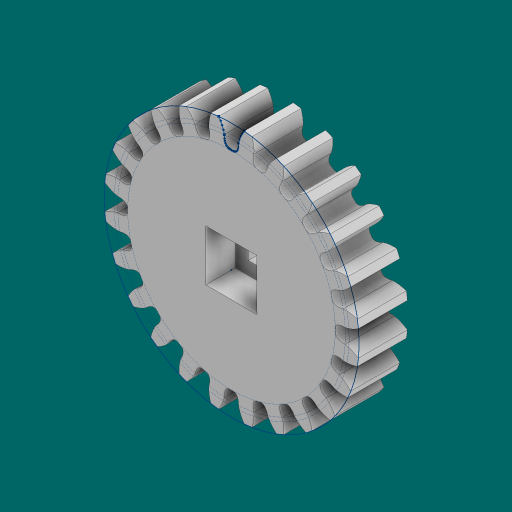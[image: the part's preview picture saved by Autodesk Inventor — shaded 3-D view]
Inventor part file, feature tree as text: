
AUTODESK INVENTOR PART (.ipt)
format: ipt  version: 2023.1 (Build 271208000, 208)  size: 313,856 bytes
history: native  units: in
note: dims shown in document units (in); Inventor stores cm internally (conversion verified against a paired STEP export)
features: extrude x4, sketch x3, pattern_circular x1
ambient origin geometry x8: Origin, YZ Plane, XZ Plane, XY Plane, X Axis, Y Axis, Z Axis, Center Point
bodies: Solid1 (feature_tree)
feature tree (8):
  sketch  "Sketch1"  dims[d0=0.25in d1=0.0in]
  extrude  "Extrusion1"  TaperAngle=0.0deg  [1 undecoded]
  extrude  "Extrusion2"  Depth=9.4488in TaperAngle=360.0deg
  pattern_circular  "Circular Pattern1"  [2 undecoded]
  extrude  "Extrusion3"  Depth=0.15in TaperAngle=0.0deg
  extrude  "Extrusion4"  Depth=0.13in
  sketch  "Sketch2"  dims[d2=0.0in d3=0.0in d4=9.4488in d5=360.0deg]
  sketch  "Sketch3"  dims[d7=0.26in d8=0.26in d9=0.15in d10=0.0in d11=0.13in d12=0.13in d13=0.0in d14=0.0in]
note: 3 required parameter values undecoded (feature->parameter linkage not recoverable at this tier; creation-order binding heuristic only, values carry confidence <= 0.55)
